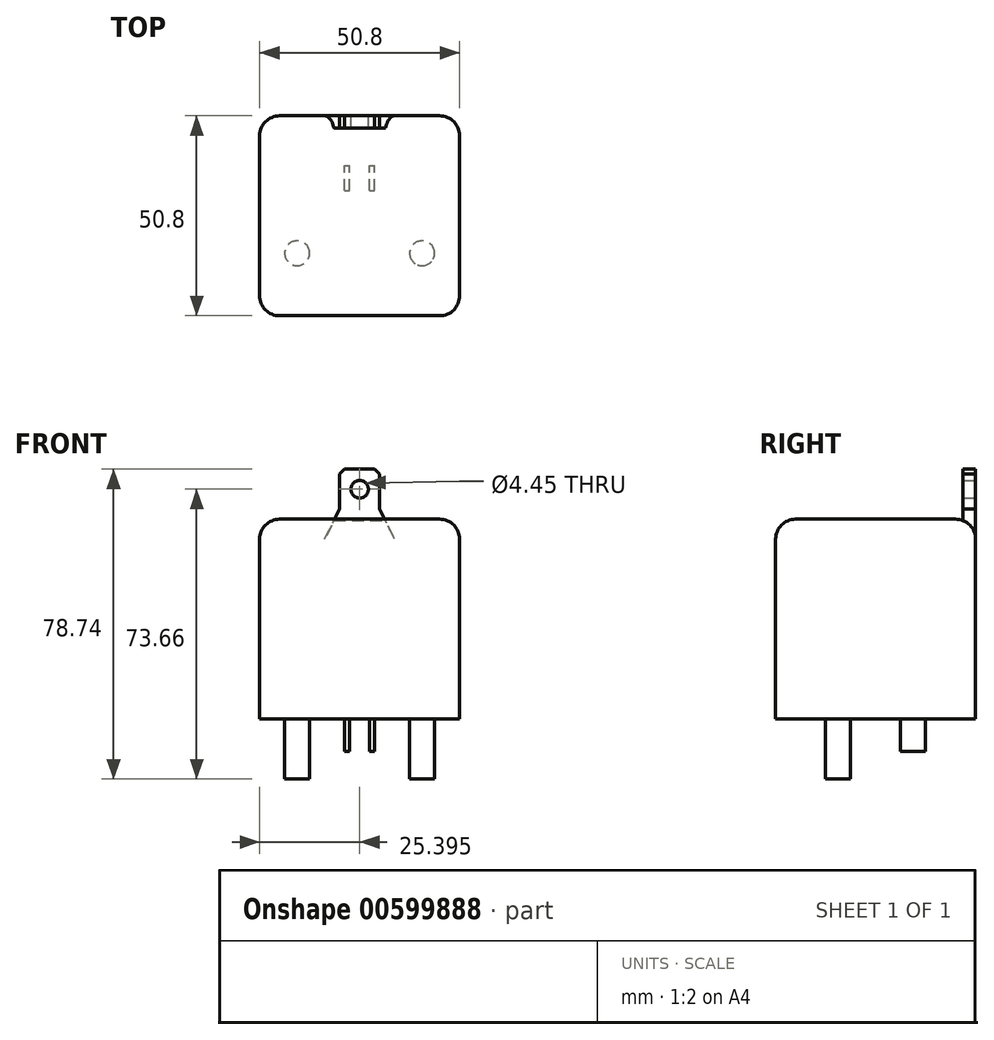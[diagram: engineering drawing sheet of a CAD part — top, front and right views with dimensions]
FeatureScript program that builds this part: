
annotation { "Feature Type Name" : "Feature", "Feature Type Description" : "" }
export const myFeature = defineFeature(function(context is Context, id is Id, definition is map)
    precondition{}
    {
        {
            var Q0;
            Q0=qCreatedBy(makeId("Top.planeOp"),FACE);
            var sketch = newSketch(context, id + "F0", { "sketchPlane" : qUnion([Q0])});
            skLineSegment(sketch, "E0.bottom", {"start": v(-30.1, -27.86) * mm, "end": v(20.7, -27.86) * mm});
            skLineSegment(sketch, "E0.top", {"start": v(-30.1, 22.94) * mm, "end": v(20.7, 22.94) * mm});
            skLineSegment(sketch, "E0.left", {"start": v(-30.1, -27.86) * mm, "end": v(-30.1, 22.94) * mm});
            skLineSegment(sketch, "E0.right", {"start": v(20.7, -27.86) * mm, "end": v(20.7, 22.94) * mm});
            skSolve(sketch);
        }
        {
            var Q0;
            Q0 = qSketchRegion(id + "F0", true);
            extrude(context, id + "F1", {"entities" : qUnion([Q0]), "depth" : 50.8 * mm, "offsetDistance" : 25.4 * mm});
        }
        {
            var Q0;
            Q0=makeQuery(id+"F1.opExtrude","SWEPT_FACE",FACE,{"disambiguationData":[OSD([sQuery(id+"F0.wireOp",EDGE,"E0.top")])]});
            var sketch = newSketch(context, id + "F2", { "sketchPlane" : qUnion([Q0])});
            skLineSegment(sketch, "E1.bottom", {"start": v(-1.66, 50.8) * mm, "end": v(11.04, 50.8) * mm});
            skLineSegment(sketch, "E1.top", {"start": v(-1.66, 63.5) * mm, "end": v(11.04, 63.5) * mm});
            skLineSegment(sketch, "E1.left", {"start": v(-1.66, 50.8) * mm, "end": v(-1.66, 63.5) * mm});
            skLineSegment(sketch, "E1.right", {"start": v(11.04, 50.8) * mm, "end": v(11.04, 63.5) * mm});
            skLineSegment(sketch, "E2.bottom", {"start": v(-0.39, 63.5) * mm, "end": v(9.77, 63.5) * mm});
            skLineSegment(sketch, "E2.top", {"start": v(-0.39, 53.34) * mm, "end": v(9.77, 53.34) * mm});
            skLineSegment(sketch, "E2.left", {"start": v(-0.39, 63.5) * mm, "end": v(-0.39, 53.34) * mm});
            skLineSegment(sketch, "E2.right", {"start": v(9.77, 63.5) * mm, "end": v(9.77, 53.34) * mm});
            skLineSegment(sketch, "E3", {"start": v(-0.39, 53.34) * mm, "end": v(-1.66, 50.8) * mm});
            skLineSegment(sketch, "E4", {"start": v(9.77, 53.34) * mm, "end": v(11.04, 50.8) * mm});
            skLineSegment(sketch, "E5", {"start": v(-0.39, 62.23) * mm, "end": v(0.88, 63.5) * mm});
            skLineSegment(sketch, "E6", {"start": v(8.5, 63.5) * mm, "end": v(9.77, 62.23) * mm});
            skCircle(sketch, "E7", {"center": v(4.7, 58.42) * mm, "radius": 2.22 * mm});
            skPoint(sketch, "E7.centerSnap0", {"position": v(9.77, 58.42) * mm});
            skPoint(sketch, "E7.centerSnap1", {"position": v(4.7, 63.5) * mm});
            skSolve(sketch);
        }
        {
            var Q0;
            {var subQ1=sQuery(id+"F2.wireOp",EDGE,"E2.top");Q0=makeQuery(id+"F2.imprint","IMPRINT",FACE,{"disambiguationData":[TD([[makeQuery(id+"F2.imprint","IMPRINT",EDGE,{"derivedFrom":subQ1}),1.0]])]});}
            var Q1;
            Q1=makeQuery(id+"F2.imprint","IMPRINT",FACE,{"disambiguationData":[TD([[makeQuery(id+"F2.imprint","IMPRINT",EDGE,{"derivedFrom":sQuery(id+"F2.wireOp",EDGE,"E1.bottom")}),-1.0]])]});
            extrude(context, id + "F3", {"entities" : qUnion([Q0, Q1]), "operationType" : NewBodyOperationType.ADD, "oppositeDirection" : true, "depth" : 3.17 * mm, "offsetDistance" : 25.4 * mm});
        }
        {
            var Q0;
            {var subQ1=sQuery(id+"F0.wireOp",EDGE,"E0.right");var subQ2=sQuery(id+"F0.wireOp",EDGE,"E0.top");Q0=makeQuery(id+"F3.boolean.opBoolean","SPLIT",EDGE,{"disambiguationData":[TD([makeQuery(id+"F1.opExtrude","SWEPT_FACE",FACE,{"disambiguationData":[OSD([subQ1])]})])],"derivedFrom":makeQuery(id+"F1.opExtrude","CAP_EDGE",EDGE,{"disambiguationData":[OSD([subQ2])],"isStart":false})});}
            fillet(context, id + "F4", {"entities" : qUnion([Q0]), "radius" : 5.08 * mm, "tangentPropagation" : true, "allowEdgeOverflow" : false});
        }
        {
            var Q0;
            Q0=makeQuery(id+"F1.opExtrude","CAP_EDGE",EDGE,{"disambiguationData":[OSD([sQuery(id+"F0.wireOp",EDGE,"E0.left")])],"isStart":false});
            var Q1;
            Q1=makeQuery(id+"F1.opExtrude","CAP_EDGE",EDGE,{"disambiguationData":[OSD([sQuery(id+"F0.wireOp",EDGE,"E0.right")])],"isStart":false});
            fillet(context, id + "F5", {"entities" : qUnion([Q0, Q1]), "radius" : 5.08 * mm, "tangentPropagation" : true, "allowEdgeOverflow" : false});
        }
        {
            var Q0;
            Q0=makeQuery(id+"F1.opExtrude","CAP_EDGE",EDGE,{"disambiguationData":[OSD([sQuery(id+"F0.wireOp",EDGE,"E0.bottom")])],"isStart":false});
            fillet(context, id + "F6", {"entities" : qUnion([Q0]), "radius" : 5.08 * mm, "tangentPropagation" : true, "allowEdgeOverflow" : false});
        }
        {
            var Q0;
            Q0=makeQuery(id+"F1.opExtrude","CAP_FACE",FACE,{"disambiguationData":[OSD([sQuery(id+"F0.wireOp",EDGE,"E0.bottom"),sQuery(id+"F0.wireOp",EDGE,"E0.top"),sQuery(id+"F0.wireOp",EDGE,"E0.left"),sQuery(id+"F0.wireOp",EDGE,"E0.right")])],"isStart":true});
            var sketch = newSketch(context, id + "F7", { "sketchPlane" : qUnion([Q0])});
            skCircle(sketch, "E8", {"center": v(-20.57, 11.99) * mm, "radius": 3.18 * mm});
            skCircle(sketch, "E9", {"center": v(11.18, 11.99) * mm, "radius": 3.18 * mm});
            skLineSegment(sketch, "E10.bottom", {"start": v(-8.5, -3.89) * mm, "end": v(-7.23, -3.89) * mm});
            skLineSegment(sketch, "E10.top", {"start": v(-8.5, -10.24) * mm, "end": v(-7.23, -10.24) * mm});
            skLineSegment(sketch, "E10.left", {"start": v(-8.5, -3.89) * mm, "end": v(-8.5, -10.24) * mm});
            skLineSegment(sketch, "E10.right", {"start": v(-7.23, -3.89) * mm, "end": v(-7.23, -10.24) * mm});
            skLineSegment(sketch, "E11.bottom", {"start": v(-2.15, -3.89) * mm, "end": v(-0.88, -3.89) * mm});
            skLineSegment(sketch, "E11.top", {"start": v(-2.15, -10.24) * mm, "end": v(-0.88, -10.24) * mm});
            skLineSegment(sketch, "E11.left", {"start": v(-2.15, -3.89) * mm, "end": v(-2.15, -10.24) * mm});
            skLineSegment(sketch, "E11.right", {"start": v(-0.88, -3.89) * mm, "end": v(-0.88, -10.24) * mm});
            skSolve(sketch);
        }
        {
            var Q0;
            Q0=makeQuery(id+"F7.imprint","IMPRINT",FACE,{"disambiguationData":[TD([[makeQuery(id+"F7.imprint","IMPRINT",EDGE,{"derivedFrom":sQuery(id+"F7.wireOp",EDGE,"E8")}),1.0]])]});
            var Q1;
            Q1=makeQuery(id+"F7.imprint","IMPRINT",FACE,{"disambiguationData":[TD([[makeQuery(id+"F7.imprint","IMPRINT",EDGE,{"derivedFrom":sQuery(id+"F7.wireOp",EDGE,"E9")}),1.0]])]});
            extrude(context, id + "F8", {"entities" : qUnion([Q0, Q1]), "operationType" : NewBodyOperationType.ADD, "depth" : 15.24 * mm, "offsetDistance" : 25.4 * mm});
        }
        {
            var Q0;
            Q0=makeQuery(id+"F7.imprint","IMPRINT",FACE,{"disambiguationData":[TD([[makeQuery(id+"F7.imprint","IMPRINT",EDGE,{"derivedFrom":sQuery(id+"F7.wireOp",EDGE,"E10.bottom")}),-1.0]])]});
            var Q1;
            Q1=makeQuery(id+"F7.imprint","IMPRINT",FACE,{"disambiguationData":[TD([[makeQuery(id+"F7.imprint","IMPRINT",EDGE,{"derivedFrom":sQuery(id+"F7.wireOp",EDGE,"E11.bottom")}),-1.0]])]});
            extrude(context, id + "F9", {"entities" : qUnion([Q0, Q1]), "operationType" : NewBodyOperationType.ADD, "depth" : 8.25 * mm, "offsetDistance" : 25.4 * mm});
        }
    });
